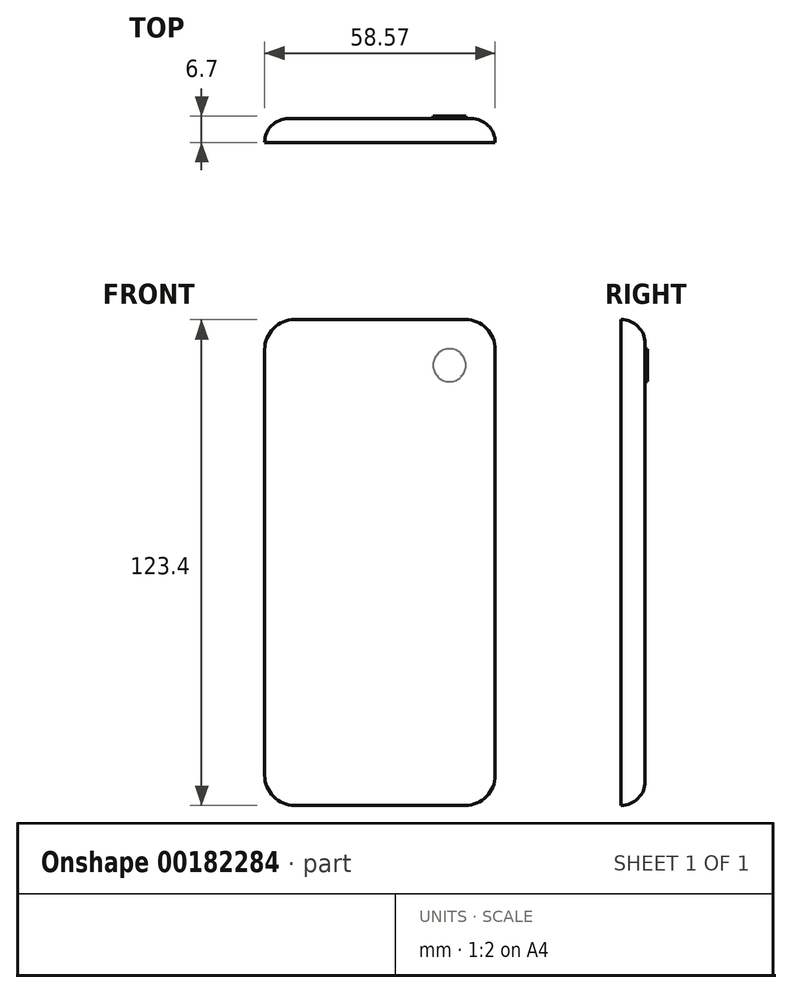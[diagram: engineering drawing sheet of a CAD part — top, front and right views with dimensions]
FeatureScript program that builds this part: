
annotation { "Feature Type Name" : "Feature", "Feature Type Description" : "" }
export const myFeature = defineFeature(function(context is Context, id is Id, definition is map)
    precondition{}
    {
        {
            var Q0;
            Q0=qCreatedBy(makeId("Front.planeOp"),FACE);
            var sketch = newSketch(context, id + "F0", { "sketchPlane" : qUnion([Q0])});
            skLineSegment(sketch, "E0.bottom", {"start": v(-34.7, 65.35) * mm, "end": v(8.62, 65.35) * mm});
            skLineSegment(sketch, "E0.top", {"start": v(-34.7, -58.05) * mm, "end": v(8.62, -58.05) * mm});
            skLineSegment(sketch, "E0.left", {"start": v(-42.33, 57.73) * mm, "end": v(-42.33, -50.43) * mm});
            skLineSegment(sketch, "E0.right", {"start": v(16.24, 57.73) * mm, "end": v(16.24, -50.43) * mm});
            skPoint(sketch, "E1.visualSharp", {"position": v(-42.33, 65.35) * mm});
            skArc(sketch, "E1.filletArc", {"start": v(-34.7, 65.35) * mm, "mid": v(-40.1, 63.12) * mm, "end": v(-42.33, 57.73) * mm});
            skPoint(sketch, "E2.visualSharp", {"position": v(16.24, 65.35) * mm});
            skArc(sketch, "E2.filletArc", {"start": v(16.24, 57.73) * mm, "mid": v(14.01, 63.12) * mm, "end": v(8.62, 65.35) * mm});
            skPoint(sketch, "E3.visualSharp", {"position": v(16.24, -58.05) * mm});
            skArc(sketch, "E3.filletArc", {"start": v(8.62, -58.05) * mm, "mid": v(14.01, -55.81) * mm, "end": v(16.24, -50.43) * mm});
            skPoint(sketch, "E4.visualSharp", {"position": v(-42.33, -58.05) * mm});
            skArc(sketch, "E4.filletArc", {"start": v(-42.33, -50.43) * mm, "mid": v(-40.1, -55.81) * mm, "end": v(-34.7, -58.05) * mm});
            skSolve(sketch);
        }
        {
            var Q0;
            Q0 = qSketchRegion(id + "F0", true);
            extrude(context, id + "F1", {"entities" : qUnion([Q0]), "depth" : 6.1 * mm});
        }
        {
            var Q0;
            Q0=makeQuery(id+"F1.opExtrude","CAP_FACE",FACE,{"disambiguationData":[OSD([sQuery(id+"F0.wireOp",EDGE,"E0.bottom"),sQuery(id+"F0.wireOp",EDGE,"E0.top"),sQuery(id+"F0.wireOp",EDGE,"E0.left"),sQuery(id+"F0.wireOp",EDGE,"E0.right"),sQuery(id+"F0.wireOp",EDGE,"E1.filletArc"),sQuery(id+"F0.wireOp",EDGE,"E2.filletArc"),sQuery(id+"F0.wireOp",EDGE,"E3.filletArc"),sQuery(id+"F0.wireOp",EDGE,"E4.filletArc")])],"isStart":true});
            fillet(context, id + "F2", {"entities" : qUnion([Q0]), "radius" : 6.1 * mm, "tangentPropagation" : true, "allowEdgeOverflow" : false});
        }
        {
            var Q0;
            Q0=makeQuery(id+"F1.opExtrude","CAP_FACE",FACE,{"disambiguationData":[OSD([sQuery(id+"F0.wireOp",EDGE,"E0.bottom"),sQuery(id+"F0.wireOp",EDGE,"E0.top"),sQuery(id+"F0.wireOp",EDGE,"E0.left"),sQuery(id+"F0.wireOp",EDGE,"E0.right"),sQuery(id+"F0.wireOp",EDGE,"E1.filletArc"),sQuery(id+"F0.wireOp",EDGE,"E2.filletArc"),sQuery(id+"F0.wireOp",EDGE,"E3.filletArc"),sQuery(id+"F0.wireOp",EDGE,"E4.filletArc")])],"isStart":true});
            var sketch = newSketch(context, id + "F3", { "sketchPlane" : qUnion([Q0])});
            skCircle(sketch, "E5", {"center": v(-4.63, 53.75) * mm, "radius": 4.18 * mm});
            skSolve(sketch);
        }
        {
            var Q0;
            Q0 = qSketchRegion(id + "F3", true);
            extrude(context, id + "F4", {"entities" : qUnion([Q0]), "operationType" : NewBodyOperationType.ADD, "depth" : .60 * mm});
        }
    });
